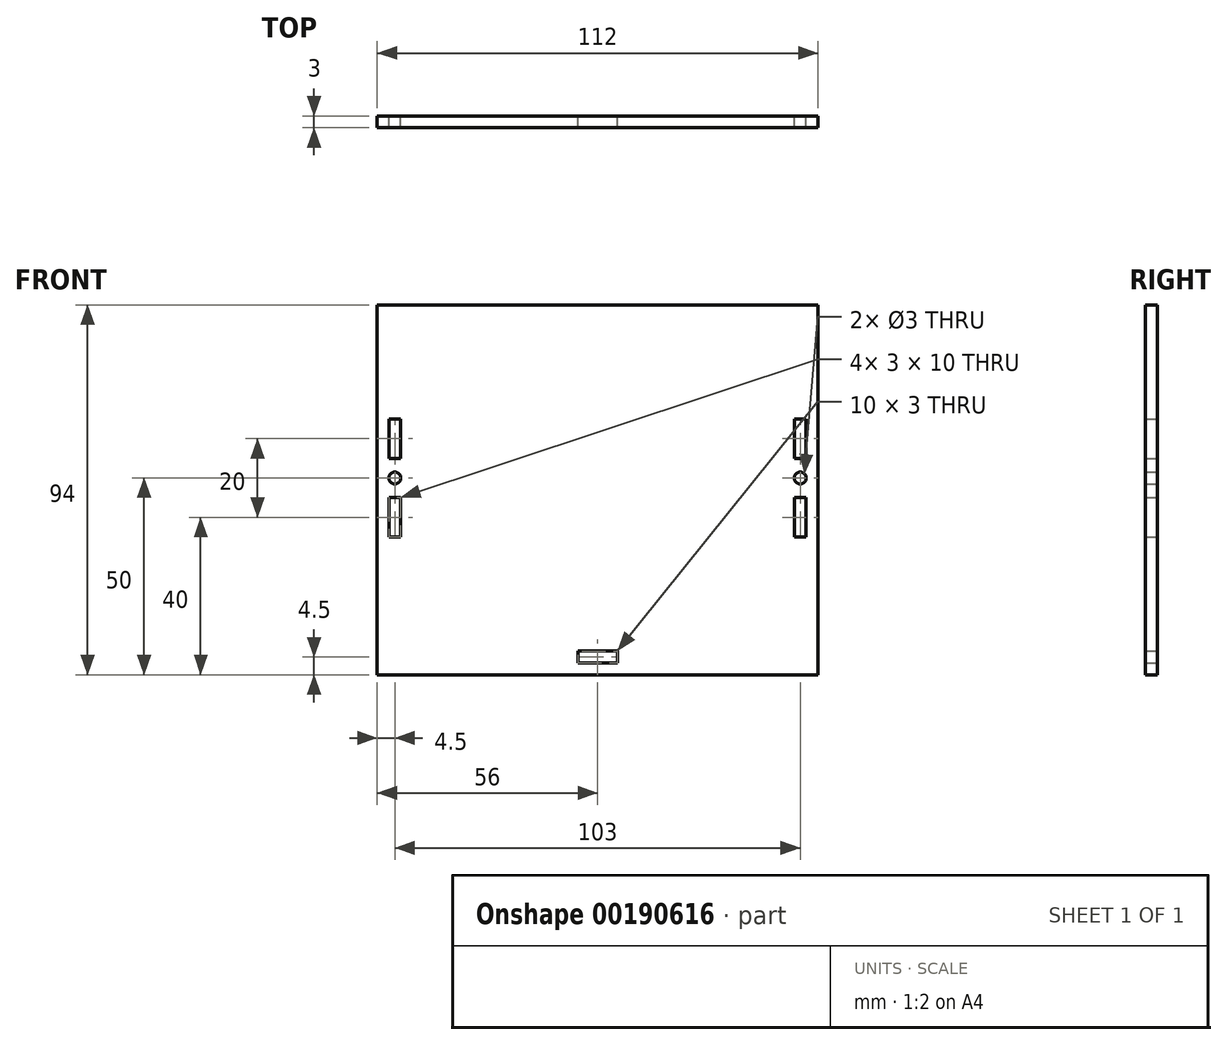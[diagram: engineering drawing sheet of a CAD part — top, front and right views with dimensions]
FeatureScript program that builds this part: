
annotation { "Feature Type Name" : "Feature", "Feature Type Description" : "" }
export const myFeature = defineFeature(function(context is Context, id is Id, definition is map)
    precondition{}
    {
        {
            var Q0;
            Q0=qCreatedBy(makeId("Front.planeOp"),FACE);
            var sketch = newSketch(context, id + "F0", { "sketchPlane" : qUnion([Q0])});
            skLineSegment(sketch, "E0.bottom", {"start": v(56, 47) * mm, "end": v(-56, 47) * mm});
            skLineSegment(sketch, "E0.top", {"start": v(56, -47) * mm, "end": v(-56, -47) * mm});
            skLineSegment(sketch, "E0.left", {"start": v(56, 47) * mm, "end": v(56, -47) * mm});
            skLineSegment(sketch, "E0.right", {"start": v(-56, 47) * mm, "end": v(-56, -47) * mm});
            skPoint(sketch, "E0.middle", {"position": v(0, 0) * mm});
            skLineSegment(sketch, "E1", {"start": v(0, 47) * mm, "end": v(0, -47) * mm, "construction": true});
            skLineSegment(sketch, "E2.bottom", {"start": v(-53, 8) * mm, "end": v(-50, 8) * mm});
            skLineSegment(sketch, "E2.top", {"start": v(-53, 18) * mm, "end": v(-50, 18) * mm});
            skLineSegment(sketch, "E2.left", {"start": v(-53, 8) * mm, "end": v(-53, 18) * mm});
            skLineSegment(sketch, "E2.right", {"start": v(-50, 8) * mm, "end": v(-50, 18) * mm});
            skLineSegment(sketch, "E3.bottom", {"start": v(5, -41) * mm, "end": v(-5, -41) * mm});
            skLineSegment(sketch, "E3.top", {"start": v(5, -44) * mm, "end": v(-5, -44) * mm});
            skLineSegment(sketch, "E3.left", {"start": v(5, -41) * mm, "end": v(5, -44) * mm});
            skLineSegment(sketch, "E3.right", {"start": v(-5, -41) * mm, "end": v(-5, -44) * mm});
            skPoint(sketch, "E3.middle", {"position": v(0, -42.5) * mm});
            skCircle(sketch, "E4", {"center": v(-51.5, 3) * mm, "radius": 1.5 * mm});
            skLineSegment(sketch, "E5.bottom", {"start": v(-53, -2) * mm, "end": v(-50, -2) * mm});
            skLineSegment(sketch, "E5.top", {"start": v(-53, -12) * mm, "end": v(-50, -12) * mm});
            skLineSegment(sketch, "E5.left", {"start": v(-53, -2) * mm, "end": v(-53, -12) * mm});
            skLineSegment(sketch, "E5.right", {"start": v(-50, -2) * mm, "end": v(-50, -12) * mm});
            skCircle(sketch, "E6.MirrorC", {"center": v(51.5, 3) * mm, "radius": 1.5 * mm});
            skLineSegment(sketch, "E7.MirrorCS", {"start": v(53, -12) * mm, "end": v(50, -12) * mm});
            skLineSegment(sketch, "E8.MirrorCS", {"start": v(50, -2) * mm, "end": v(50, -12) * mm});
            skLineSegment(sketch, "E9.MirrorCS", {"start": v(53, -2) * mm, "end": v(50, -2) * mm});
            skLineSegment(sketch, "E10.MirrorCS", {"start": v(53, -2) * mm, "end": v(53, -12) * mm});
            skLineSegment(sketch, "E11.MirrorCS", {"start": v(53, 8) * mm, "end": v(50, 8) * mm});
            skLineSegment(sketch, "E12.MirrorCS", {"start": v(53, 8) * mm, "end": v(53, 18) * mm});
            skLineSegment(sketch, "E13.MirrorCS", {"start": v(53, 18) * mm, "end": v(50, 18) * mm});
            skLineSegment(sketch, "E14.MirrorCS", {"start": v(50, 8) * mm, "end": v(50, 18) * mm});
            skSolve(sketch);
        }
        {
            var Q0;
            Q0=makeQuery(id+"F0.imprint","IMPRINT",FACE,{"disambiguationData":[TD([[makeQuery(id+"F0.imprint","IMPRINT",EDGE,{"derivedFrom":sQuery(id+"F0.wireOp",EDGE,"E0.bottom")}),1.0]])]});
            extrude(context, id + "F1", {"entities" : qUnion([Q0]), "depth" : 3 * mm});
        }
    });
